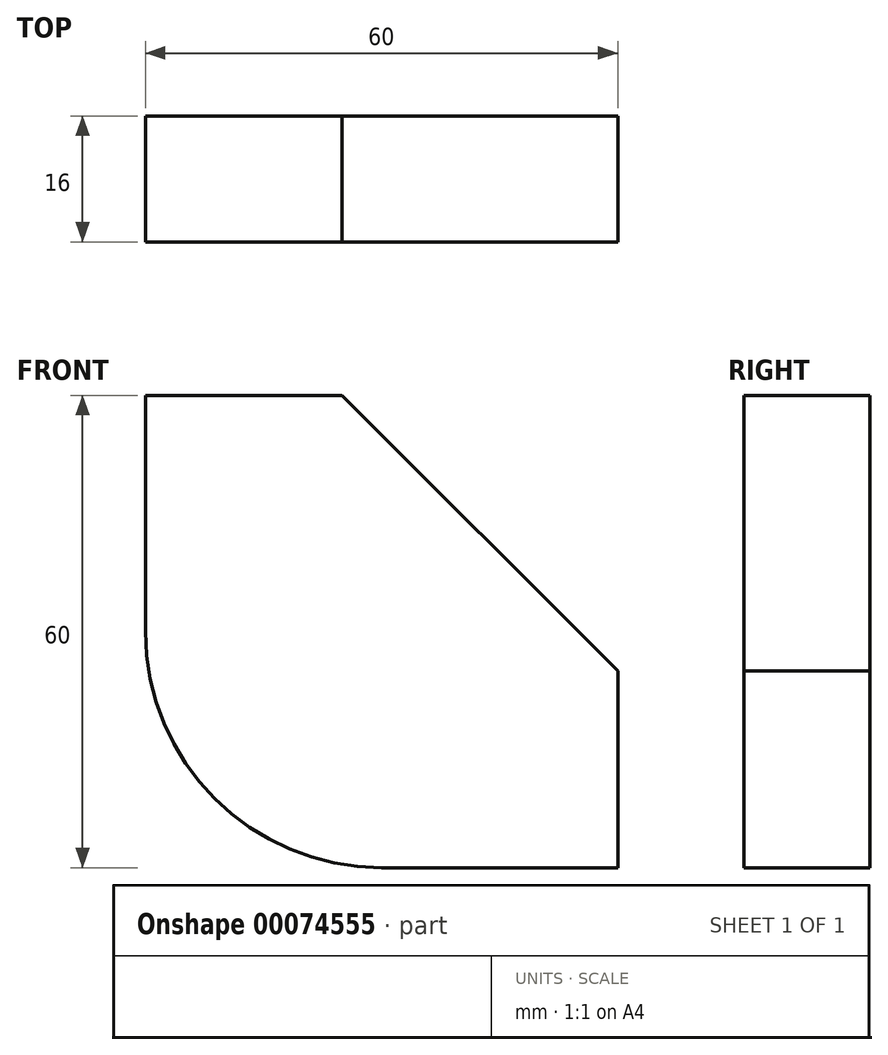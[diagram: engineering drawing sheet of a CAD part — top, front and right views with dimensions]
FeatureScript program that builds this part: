
annotation { "Feature Type Name" : "Feature", "Feature Type Description" : "" }
export const myFeature = defineFeature(function(context is Context, id is Id, definition is map)
    precondition{}
    {
        {
            var Q0;
            Q0=qCreatedBy(makeId("Front.planeOp"),FACE);
            var sketch = newSketch(context, id + "F0", { "sketchPlane" : qUnion([Q0])});
            skLineSegment(sketch, "E0", {"start": v(0, 0) * mm, "end": v(-25, 0) * mm});
            skLineSegment(sketch, "E1", {"start": v(-25, 0) * mm, "end": v(-25, -30) * mm});
            skLineSegment(sketch, "E2", {"start": v(5, -60) * mm, "end": v(35, -60) * mm});
            skLineSegment(sketch, "E3", {"start": v(35, -60) * mm, "end": v(35, -35) * mm});
            skLineSegment(sketch, "E4", {"start": v(35, -35) * mm, "end": v(0, 0) * mm});
            skPoint(sketch, "E5.visualSharp", {"position": v(-25, -60) * mm});
            skArc(sketch, "E5.filletArc", {"start": v(-25, -30) * mm, "mid": v(-16.21, -51.21) * mm, "end": v(5, -60) * mm});
            skSolve(sketch);
        }
        {
            var Q0;
            Q0 = qSketchRegion(id + "F0", true);
            extrude(context, id + "F1", {"entities" : qUnion([Q0]), "depth" : 16 * mm});
        }
    });
